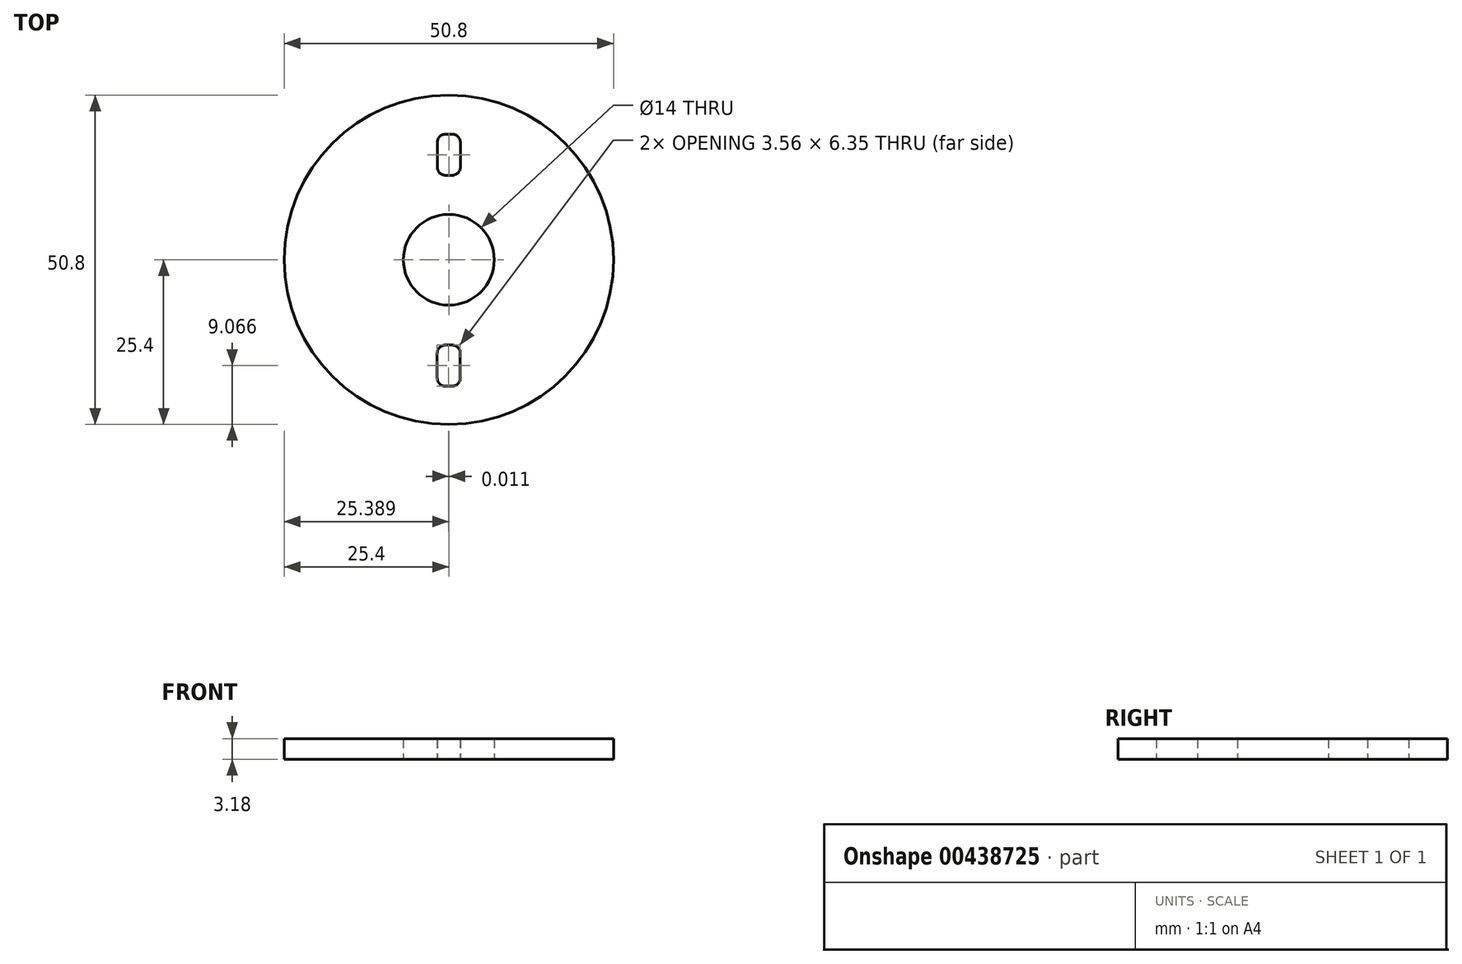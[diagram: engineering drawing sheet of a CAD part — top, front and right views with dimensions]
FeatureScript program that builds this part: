
annotation { "Feature Type Name" : "Feature", "Feature Type Description" : "" }
export const myFeature = defineFeature(function(context is Context, id is Id, definition is map)
    precondition{}
    {
        {
            var Q0;
            Q0=qCreatedBy(makeId("Top.planeOp"),FACE);
            var sketch = newSketch(context, id + "F0", { "sketchPlane" : qUnion([Q0])});
            skCircle(sketch, "E0", {"center": v(0, 0) * mm, "radius": 25.4 * mm});
            skCircle(sketch, "E1", {"center": v(0, 0) * mm, "radius": 7 * mm});
            skLineSegment(sketch, "E2", {"start": v(0, 25.4) * mm, "end": v(0, 7) * mm, "construction": true});
            skLineSegment(sketch, "E3", {"start": v(0, -7) * mm, "end": v(-0.02, -25.4) * mm, "construction": true});
            skLineSegment(sketch, "E4.bottom", {"start": v(0.5, 19.38) * mm, "end": v(-0.5, 19.38) * mm});
            skLineSegment(sketch, "E4.top", {"start": v(0.5, 13.02) * mm, "end": v(-0.5, 13.02) * mm});
            skLineSegment(sketch, "E4.left", {"start": v(1.78, 18.1) * mm, "end": v(1.78, 14.3) * mm});
            skLineSegment(sketch, "E4.right", {"start": v(-1.78, 18.1) * mm, "end": v(-1.78, 14.3) * mm});
            skPoint(sketch, "E4.middle", {"position": v(0, 16.2) * mm});
            skPoint(sketch, "E5.visualSharp", {"position": v(-1.78, 19.38) * mm});
            skArc(sketch, "E5.filletArc", {"start": v(-0.5, 19.38) * mm, "mid": v(-1.4, 19) * mm, "end": v(-1.78, 18.1) * mm});
            skPoint(sketch, "E6.visualSharp", {"position": v(1.78, 19.38) * mm});
            skArc(sketch, "E6.filletArc", {"start": v(1.78, 18.1) * mm, "mid": v(1.4, 19) * mm, "end": v(0.5, 19.38) * mm});
            skPoint(sketch, "E7.visualSharp", {"position": v(-1.78, 13.02) * mm});
            skArc(sketch, "E7.filletArc", {"start": v(-1.78, 14.3) * mm, "mid": v(-1.4, 13.4) * mm, "end": v(-0.5, 13.02) * mm});
            skPoint(sketch, "E8.visualSharp", {"position": v(1.78, 13.02) * mm});
            skArc(sketch, "E8.filletArc", {"start": v(0.5, 13.02) * mm, "mid": v(1.4, 13.4) * mm, "end": v(1.78, 14.3) * mm});
            skLineSegment(sketch, "E9", {"start": v(-25.4, 0) * mm, "end": v(25.4, 0) * mm, "construction": true});
            skLineSegment(sketch, "E10.bottom", {"start": v(0.5, -13.16) * mm, "end": v(-0.52, -13.16) * mm});
            skLineSegment(sketch, "E10.top", {"start": v(0.5, -19.5) * mm, "end": v(-0.52, -19.5) * mm});
            skLineSegment(sketch, "E10.left", {"start": v(1.77, -14.43) * mm, "end": v(1.77, -18.24) * mm});
            skLineSegment(sketch, "E10.right", {"start": v(-1.79, -14.43) * mm, "end": v(-1.79, -18.24) * mm});
            skPoint(sketch, "E10.middle", {"position": v(-0.01, -16.33) * mm});
            skPoint(sketch, "E11.visualSharp", {"position": v(-1.79, -19.5) * mm});
            skArc(sketch, "E11.filletArc", {"start": v(-1.79, -18.24) * mm, "mid": v(-1.42, -19.14) * mm, "end": v(-0.52, -19.5) * mm});
            skPoint(sketch, "E12.visualSharp", {"position": v(1.77, -19.5) * mm});
            skArc(sketch, "E12.filletArc", {"start": v(0.5, -19.5) * mm, "mid": v(1.4, -19.14) * mm, "end": v(1.77, -18.24) * mm});
            skPoint(sketch, "E13.visualSharp", {"position": v(1.77, -13.16) * mm});
            skArc(sketch, "E13.filletArc", {"start": v(1.77, -14.43) * mm, "mid": v(1.4, -13.53) * mm, "end": v(0.5, -13.16) * mm});
            skPoint(sketch, "E14.visualSharp", {"position": v(-1.79, -13.16) * mm});
            skArc(sketch, "E14.filletArc", {"start": v(-0.52, -13.16) * mm, "mid": v(-1.42, -13.53) * mm, "end": v(-1.79, -14.43) * mm});
            skSolve(sketch);
        }
        {
            var Q0;
            Q0=makeQuery(id+"F0.imprint","IMPRINT",FACE,{"disambiguationData":[TD([[makeQuery(id+"F0.imprint","IMPRINT",EDGE,{"derivedFrom":sQuery(id+"F0.wireOp",EDGE,"E0")}),1.0]])]});
            extrude(context, id + "F1", {"entities" : qUnion([Q0]), "depth" : 3.17 * mm});
        }
    });
